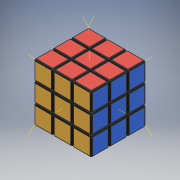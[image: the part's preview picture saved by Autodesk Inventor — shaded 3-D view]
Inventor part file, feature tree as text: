
AUTODESK INVENTOR PART (.ipt)
format: ipt  version: 2017 (Build 210142000, 142)  size: 1,125,888 bytes
history: native  units: mm
features: other x48, plane x3
ambient origin geometry x8: Origin, YZ Plane, XZ Plane, XY Plane, X Axis, Y Axis, Z Axis, Center Point
bodies: Solid1 (feature_tree), Solid2 (feature_tree), Solid3 (feature_tree), Solid4 (feature_tree), Solid5 (feature_tree), Solid6 (feature_tree), Solid7 (feature_tree), Solid8 (feature_tree), Solid9 (feature_tree), Solid10 (feature_tree), Solid11 (feature_tree), Solid12 (feature_tree), Solid13 (feature_tree), Solid14 (feature_tree), Solid15 (feature_tree), Solid16 (feature_tree), Solid17 (feature_tree), Solid18 (feature_tree), Solid19 (feature_tree), Solid20 (feature_tree), Solid21 (feature_tree), Solid22 (feature_tree), Solid23 (feature_tree), Solid24 (feature_tree), Solid25 (feature_tree), Solid26 (feature_tree), Solid27 (feature_tree)
feature tree (51):
  other  "Cube.ipt"
  plane  "Work Plane1"
  plane  "Work Plane2"
  plane  "Work Plane3"
  other  "Solid1::Cube.ipt"
  other  "Solid2::Cube.ipt"
  other  "Solid3::Cube.ipt"
  other  "Solid4::Cube.ipt"
  other  "Solid5::Cube.ipt"
  other  "Solid6::Cube.ipt"
  other  "Solid7::Cube.ipt"
  other  "Solid8::Cube.ipt"
  other  "Solid9::Cube.ipt"
  other  "Solid10::Cube.ipt"
  other  "Solid11::Cube.ipt"
  other  "Solid12::Cube.ipt"
  other  "Solid13::Cube.ipt"
  other  "Solid14::Cube.ipt"
  other  "Solid15::Cube.ipt"
  other  "Solid16::Cube.ipt"
  other  "Solid17::Cube.ipt"
  other  "Solid18::Cube.ipt"
  other  "Solid19::Cube.ipt"
  other  "Solid20::Cube.ipt"
  other  "Solid21::Cube.ipt"
  other  "Solid22::Cube.ipt"
  other  "Solid23::Cube.ipt"
  other  "Solid24::Cube.ipt"
  other  "Solid25::Cube.ipt"
  other  "Solid26::Cube.ipt"
  other  "Solid27::Cube.ipt"
  other  "TaggingFeature1"
  other  "Work Axis1"
  other  "Work Axis2"
  other  "Work Axis3"
  other  "Work Axis4"
  other  "Work Axis5"
  other  "Work Axis6"
  other  "Work Axis7"
  other  "Work Point1"
  other  "Work Point2"
  other  "Work Point3"
  other  "Work Point4"
  other  "Work Point5"
  other  "Work Point6"
  other  "Work Point7"
  other  "Work Point8"
  other  "Work Point9"
  other  "Work Point10"
  other  "Work Point11"
  other  "Work Point12"
